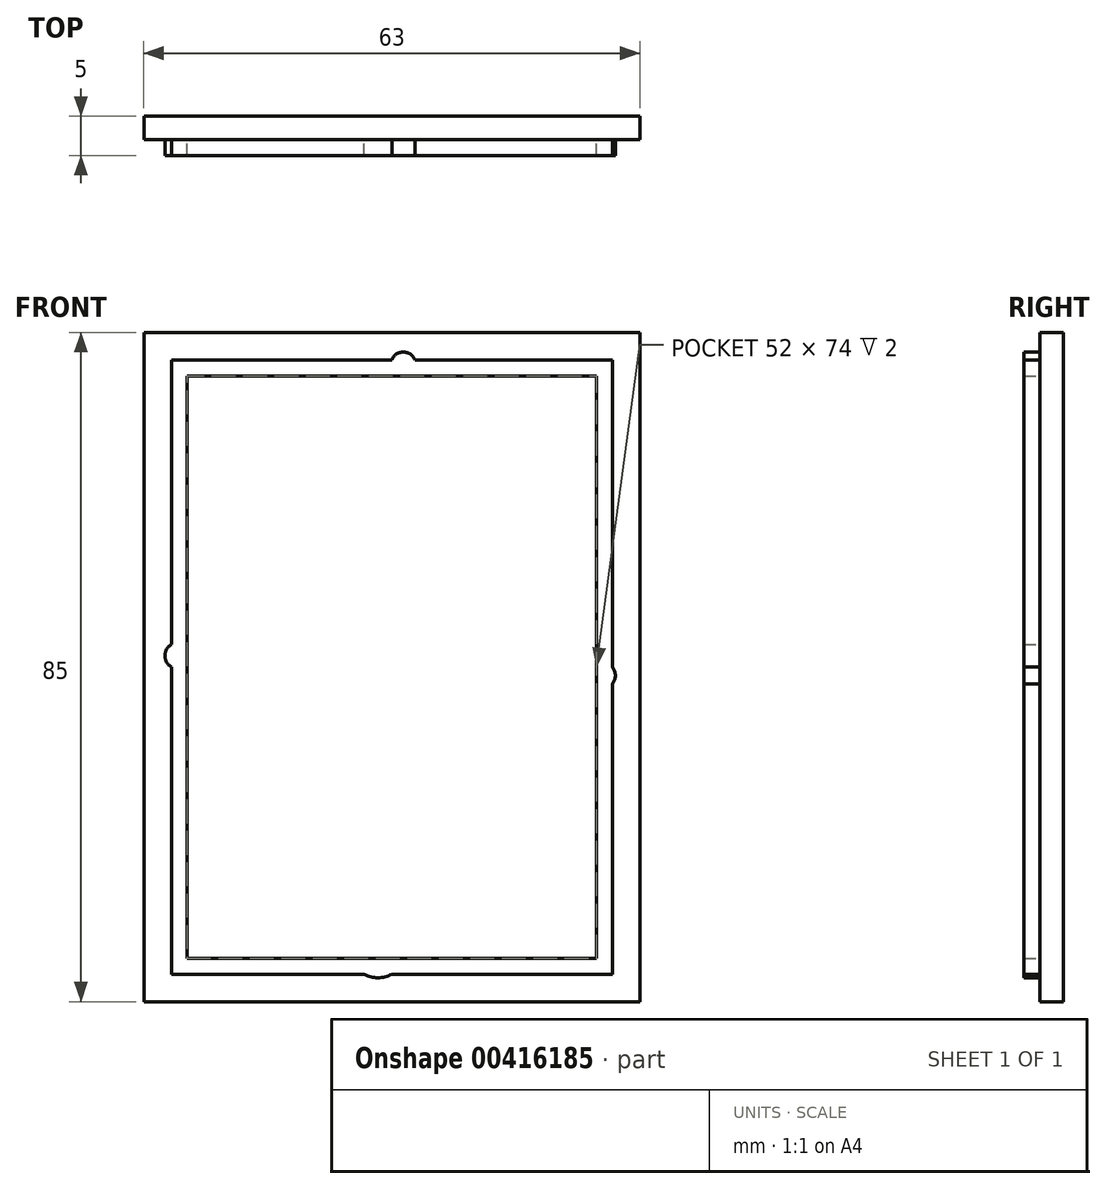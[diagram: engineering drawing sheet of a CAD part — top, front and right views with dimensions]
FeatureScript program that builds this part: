
annotation { "Feature Type Name" : "Feature", "Feature Type Description" : "" }
export const myFeature = defineFeature(function(context is Context, id is Id, definition is map)
    precondition{}
    {
        {
            var Q0;
            Q0=qCreatedBy(makeId("Front.planeOp"),FACE);
            var sketch = newSketch(context, id + "F0", { "sketchPlane" : qUnion([Q0])});
            skLineSegment(sketch, "E0.bottom", {"start": v(-12.38, 48.08) * mm, "end": v(50.62, 48.08) * mm});
            skLineSegment(sketch, "E0.top", {"start": v(-12.38, -36.92) * mm, "end": v(50.62, -36.92) * mm});
            skLineSegment(sketch, "E0.left", {"start": v(-12.38, 48.08) * mm, "end": v(-12.38, -36.92) * mm});
            skLineSegment(sketch, "E0.right", {"start": v(50.62, 48.08) * mm, "end": v(50.62, -36.92) * mm});
            skLineSegment(sketch, "E1.bottom", {"start": v(47.12, -33.42) * mm, "end": v(19.12, -33.42) * mm});
            skLineSegment(sketch, "E1.top", {"start": v(47.12, 44.58) * mm, "end": v(22.05, 44.58) * mm});
            skLineSegment(sketch, "E1.left", {"start": v(47.12, -33.42) * mm, "end": v(47.12, 3.44) * mm});
            skLineSegment(sketch, "E1.right", {"start": v(-8.88, -33.42) * mm, "end": v(-8.88, 5.58) * mm});
            skLineSegment(sketch, "E2.bottom", {"start": v(-6.88, 42.58) * mm, "end": v(45.12, 42.58) * mm});
            skLineSegment(sketch, "E2.top", {"start": v(-6.88, -31.42) * mm, "end": v(45.12, -31.42) * mm});
            skLineSegment(sketch, "E2.left", {"start": v(-6.88, 42.58) * mm, "end": v(-6.88, -31.42) * mm});
            skLineSegment(sketch, "E2.right", {"start": v(45.12, 42.58) * mm, "end": v(45.12, -31.42) * mm});
            skArc(sketch, "E3", {"start": v(-8.88, 8.48) * mm, "mid": v(-9.7, 7.03) * mm, "end": v(-8.88, 5.58) * mm});
            skPoint(sketch, "E4.endSnap0", {"position": v(19.12, 48.08) * mm});
            skArc(sketch, "E5", {"start": v(47.12, 3.44) * mm, "mid": v(47.52, 4.5) * mm, "end": v(47.12, 5.58) * mm});
            skPoint(sketch, "E5.endSnap0", {"position": v(45.12, 5.58) * mm});
            skArc(sketch, "E6", {"start": v(15.6, -33.42) * mm, "mid": v(17.36, -33.89) * mm, "end": v(19.12, -33.42) * mm});
            skLineSegment(sketch, "E7.trimOffspring", {"start": v(19.12, 44.58) * mm, "end": v(-8.88, 44.58) * mm});
            skLineSegment(sketch, "E8.trimOffspring", {"start": v(47.12, 5.58) * mm, "end": v(47.12, 44.58) * mm});
            skLineSegment(sketch, "E9.trimOffspring", {"start": v(15.6, -33.42) * mm, "end": v(-8.88, -33.42) * mm});
            skLineSegment(sketch, "E10.trimOffspring", {"start": v(-8.88, 8.48) * mm, "end": v(-8.88, 44.58) * mm});
            skArc(sketch, "E11", {"start": v(22.05, 44.58) * mm, "mid": v(20.58, 45.62) * mm, "end": v(19.12, 44.58) * mm});
            skLineSegment(sketch, "E12.trimOffspring", {"start": v(19.12, 44.58) * mm, "end": v(16, 44.58) * mm});
            skSolve(sketch);
        }
        {
            var Q0;
            Q0=makeQuery(id+"F0.imprint","IMPRINT",FACE,{"disambiguationData":[TD([[makeQuery(id+"F0.imprint","IMPRINT",EDGE,{"derivedFrom":sQuery(id+"F0.wireOp",EDGE,"E2.bottom")}),1.0]])]});
            extrude(context, id + "F1", {"entities" : qUnion([Q0]), "depth" : 5 * mm});
        }
        {
            var Q0;
            Q0=makeQuery(id+"F0.imprint","IMPRINT",FACE,{"disambiguationData":[TD([[makeQuery(id+"F0.imprint","IMPRINT",EDGE,{"derivedFrom":sQuery(id+"F0.wireOp",EDGE,"E0.bottom")}),-1.0]])]});
            var Q1;
            Q1=makeQuery(id+"F0.imprint","IMPRINT",FACE,{"disambiguationData":[TD([[makeQuery(id+"F0.imprint","IMPRINT",EDGE,{"derivedFrom":sQuery(id+"F0.wireOp",EDGE,"E2.bottom")}),-1.0]])]});
            extrude(context, id + "F2", {"entities" : qUnion([Q0, Q1]), "operationType" : NewBodyOperationType.ADD, "depth" : 3 * mm});
        }
    });
